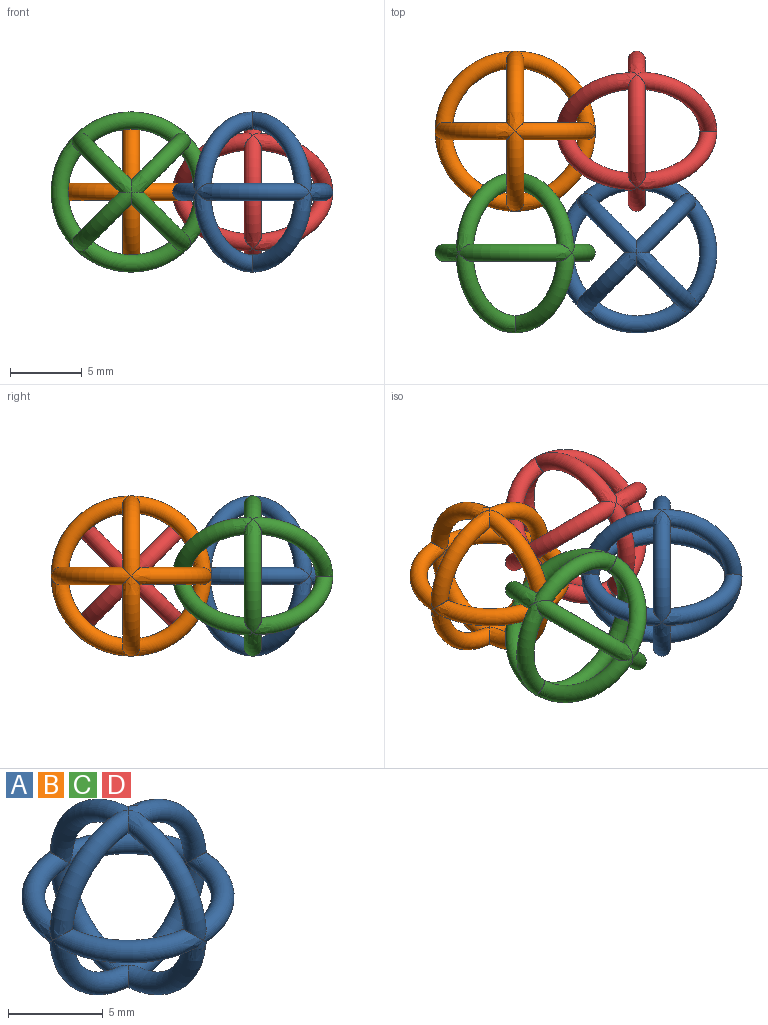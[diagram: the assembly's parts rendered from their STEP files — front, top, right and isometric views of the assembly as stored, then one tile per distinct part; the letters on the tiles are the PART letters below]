
ASSEMBLY  parts=4 mates=3
PART A: 12 faces, bbox 12.1x12.1x12.1 mm
  f0: torus R=5mm, axis (1,0,0), area 26.7mm2, adj f1,f3,f4,f11
  f1: torus R=5mm, axis (0,0,-1), area 26.7mm2, adj f0,f2,f10,f11
  f2: torus R=5mm, axis (1,0,0), area 26.7mm2, adj f1,f3,f9,f10
  f3: torus R=5mm, axis (0,0,-1), area 26.7mm2, adj f0,f2,f4,f9
  f4: torus R=5mm, axis (0,1,0), area 26.7mm2, adj f0,f3,f5,f8
  f5: torus R=5mm, axis (0,0,-1), area 26.7mm2, adj f4,f6,f8,f9
  f6: torus R=5mm, axis (1,0,0), area 26.7mm2, adj f5,f7,f9,f10
  f7: torus R=5mm, axis (0,0,-1), area 26.7mm2, adj f6,f8,f10,f11
  f8: torus R=5mm, axis (1,0,0), area 26.7mm2, adj f4,f5,f7,f11
  f9: torus R=5mm, axis (0,1,0), area 26.7mm2, adj f2,f3,f5,f6
  f10: torus R=5mm, axis (0,1,0), area 26.7mm2, adj f1,f2,f6,f7
  f11: torus R=5mm, axis (0,1,0), area 26.7mm2, adj f0,f1,f7,f8
PART B: same geometry as A
PART C: same geometry as A
PART D: same geometry as A
PLACE A rot(axis=(-0.36,-0.86,-0.36),98.4deg) t=(14.63,-8.5,0)mm
PLACE B rot(axis=(0.71,0,0.71),180deg) t=(6.13,0,0)mm
PLACE C rot(axis=(0.38,0,0.92),180deg) t=(6.13,-8.5,0)mm
PLACE D rot(axis=(0.68,0.28,0.68),148.6deg) t=(14.63,0,0)mm fixed
MATE planar A.f0 <-> B.f0  axis (0,0,1) through (14.63,-8.5,0)mm
MATE revolute C.f4 <-> B.f4  axis (0,-1,0) through (6.13,-8.5,0)mm
MATE revolute D.f1 <-> B.f1  axis (1,0,0) through (14.63,0,0)mm
